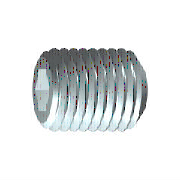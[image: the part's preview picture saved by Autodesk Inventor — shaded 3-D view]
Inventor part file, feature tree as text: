
AUTODESK INVENTOR PART (.ipt)
format: ipt  version: 2025 (Build 290162010, 162A)  size: 167,936 bytes
history: native  units: mm (DEFAULTED — no unit token found)
features: extrude x1, other x1, plane x1
ambient origin geometry x8: Origin, YZ Plane, XZ Plane, XY Plane, X Axis, Y Axis, Z Axis, Center Point
bodies: Solid1 (feature_tree), Body (feature_tree)
feature tree (3):
  extrude  "Slot"  Depth=2.0mm
  other  "Work Axis1"
  plane  "Work Plane1"
